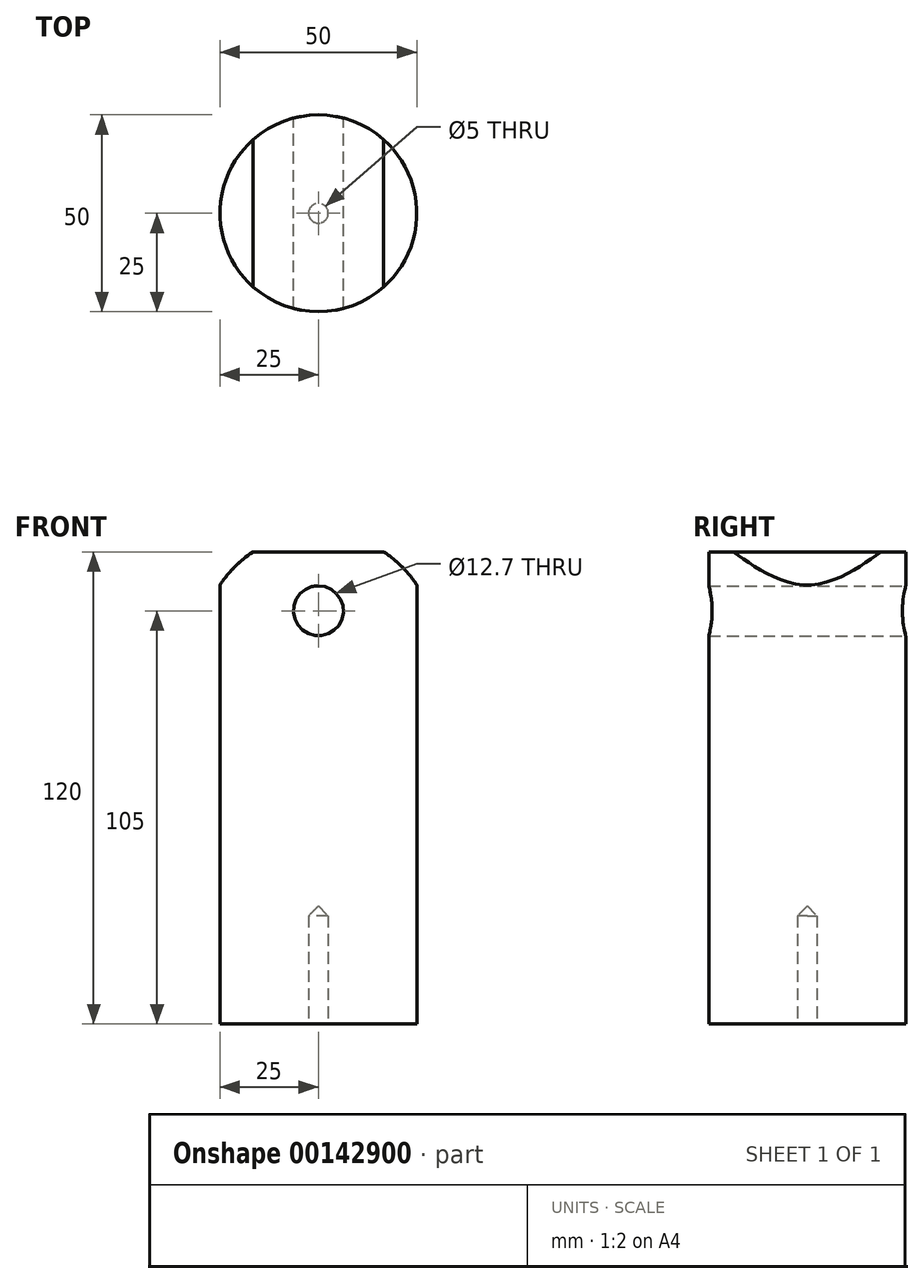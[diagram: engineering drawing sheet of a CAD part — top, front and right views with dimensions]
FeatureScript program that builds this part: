
annotation { "Feature Type Name" : "Feature", "Feature Type Description" : "" }
export const myFeature = defineFeature(function(context is Context, id is Id, definition is map)
    precondition{}
    {
        {
            var Q0;
            Q0=qCreatedBy(makeId("Top.planeOp"),FACE);
            var sketch = newSketch(context, id + "F0", { "sketchPlane" : qUnion([Q0])});
            skCircle(sketch, "E0", {"center": v(0, 0) * mm, "radius": 25 * mm});
            skCircle(sketch, "E1", {"center": v(0, 0) * mm, "radius": 2.5 * mm});
            skSolve(sketch);
        }
        {
            var Q0;
            Q0=makeQuery(id+"F0.imprint","IMPRINT",FACE,{"disambiguationData":[TD([[makeQuery(id+"F0.imprint","IMPRINT",EDGE,{"derivedFrom":sQuery(id+"F0.wireOp",EDGE,"E0")}),1.0]])]});
            var Q1;
            Q1=makeQuery(id+"F0.imprint","IMPRINT",FACE,{"disambiguationData":[TD([[makeQuery(id+"F0.imprint","IMPRINT",EDGE,{"derivedFrom":sQuery(id+"F0.wireOp",EDGE,"E1")}),1.0]])]});
            extrude(context, id + "F1", {"entities" : qUnion([Q0, Q1]), "depth" : 120 * mm});
        }
        {
            var Q0;
            Q0=makeQuery(id+"F0.imprint","IMPRINT",FACE,{"disambiguationData":[TD([[makeQuery(id+"F0.imprint","IMPRINT",EDGE,{"derivedFrom":sQuery(id+"F0.wireOp",EDGE,"E1")}),1.0]])]});
            extrude(context, id + "F2", {"entities" : qUnion([Q0]), "operationType" : NewBodyOperationType.REMOVE, "depth" : 30 * mm});
        }
        {
            var Q0;
            Q0=makeQuery(id+"F2.boolean.opBoolean","COPY",EDGE,{"derivedFrom":makeQuery(id+"F2.opExtrude","CAP_EDGE",EDGE,{"disambiguationData":[OSD([sQuery(id+"F0.wireOp",EDGE,"E1")])],"isStart":false})});
            chamfer(context, id + "F3", {"entities" : qUnion([Q0]), "width" : 2.5 * mm, "tangentPropagation" : true});
        }
        {
            var Q0;
            Q0=qCreatedBy(makeId("Front.planeOp"),FACE);
            var sketch = newSketch(context, id + "F4", { "sketchPlane" : qUnion([Q0])});
            skCircle(sketch, "E2", {"center": v(0, 105) * mm, "radius": 6.35 * mm});
            skArc(sketch, "E3", {"start": v(30, 95) * mm, "mid": v(0, 125) * mm, "end": v(-30, 95) * mm});
            skLineSegment(sketch, "E4.bottom", {"start": v(-49.44, 95) * mm, "end": v(-30, 95) * mm});
            skLineSegment(sketch, "E4.top", {"start": v(-49.44, 154.92) * mm, "end": v(51.99, 154.92) * mm});
            skLineSegment(sketch, "E4.left", {"start": v(-49.44, 95) * mm, "end": v(-49.44, 154.92) * mm});
            skLineSegment(sketch, "E4.right", {"start": v(51.99, 95) * mm, "end": v(51.99, 154.92) * mm});
            skLineSegment(sketch, "E5.trimOffspring", {"start": v(30, 95) * mm, "end": v(51.99, 95) * mm});
            skSolve(sketch);
        }
        {
            var Q0;
            Q0=qSketchRegion(id+"F4",true);
            extrude(context, id + "F5", {"entities" : qUnion([Q0]), "operationType" : NewBodyOperationType.REMOVE, "endBound" : BoundingType.THROUGH_ALL, "depth" : 25 * mm, "hasSecondDirection" : true, "secondDirectionOppositeDirection" : true, "secondDirectionDepth" : 25 * mm});
        }
    });
